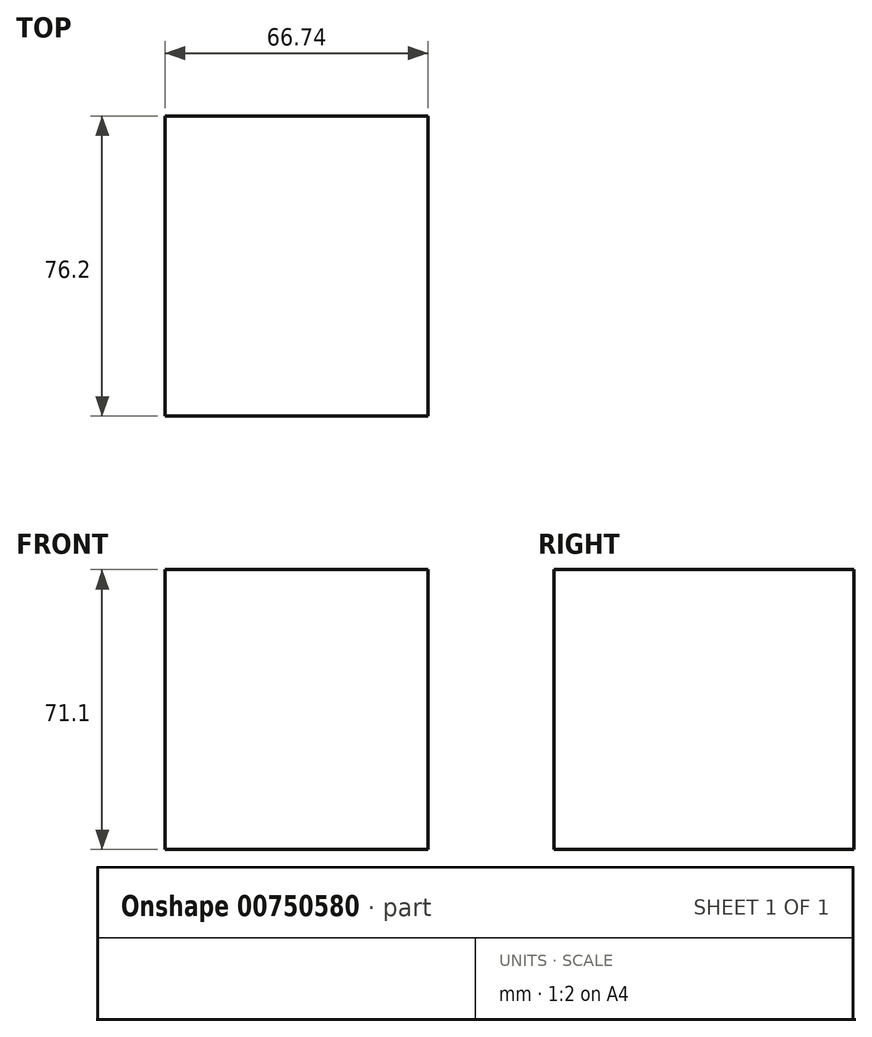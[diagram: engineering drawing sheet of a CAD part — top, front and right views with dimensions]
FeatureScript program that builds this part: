
annotation { "Feature Type Name" : "Feature", "Feature Type Description" : "" }
export const myFeature = defineFeature(function(context is Context, id is Id, definition is map)
    precondition{}
    {
        {
            var Q0;
            Q0=qCreatedBy(makeId("Front.planeOp"),FACE);
            var sketch = newSketch(context, id + "F0", { "sketchPlane" : qUnion([Q0])});
            skLineSegment(sketch, "E0.bottom", {"start": v(-32.14, 37.45) * mm, "end": v(34.6, 37.45) * mm});
            skLineSegment(sketch, "E0.top", {"start": v(-32.14, -33.65) * mm, "end": v(34.6, -33.65) * mm});
            skLineSegment(sketch, "E0.left", {"start": v(-32.14, 37.45) * mm, "end": v(-32.14, -33.65) * mm});
            skLineSegment(sketch, "E0.right", {"start": v(34.6, 37.45) * mm, "end": v(34.6, -33.65) * mm});
            skSolve(sketch);
        }
        {
            var Q0;
            Q0=makeQuery(id+"F0.imprint","IMPRINT",FACE,{"disambiguationData":[TD([[makeQuery(id+"F0.imprint","IMPRINT",EDGE,{"derivedFrom":sQuery(id+"F0.wireOp",EDGE,"E0.bottom")}),-1.0]])]});
            extrude(context, id + "F1", {"entities" : qUnion([Q0]), "oppositeDirection" : true, "depth" : 76.2 * mm, "offsetDistance" : 25.4 * mm});
        }
    });
